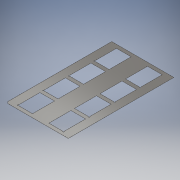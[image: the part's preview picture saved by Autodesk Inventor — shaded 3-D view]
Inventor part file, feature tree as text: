
AUTODESK INVENTOR PART (.ipt)
format: ipt  version: 2019.4 (Build 234330000, 330)  size: 232,960 bytes
history: native  units: in
note: dims shown in document units (in); Inventor stores cm internally (conversion verified against a paired STEP export)
features: extrude x2, sketch x2, chamfer x1
ambient origin geometry x8: Origin, YZ Plane, XZ Plane, XY Plane, X Axis, Y Axis, Z Axis, Center Point
bodies: Solid1 (feature_tree)
feature tree (5):
  extrude  "Extrusion1"  Depth=5.0in
  extrude  "Extrusion2"  Depth=1.1811in
  chamfer  "Chamfer1"  Distance=1.7717in
  sketch  "Sketch1"  dims[d0=8.5in d1=5.0in]
  sketch  "Sketch2"  dims[d2=0.0039in d3=0.0in d4=1.1811in d5=1.7717in d6=0.2835in d7=0.659in d8=0.0787in d9=0.0079in d18=0.0in d19=0.0in d20=0.0079in d21=1.5748in d23=2.0551in d24=0.7874in d26=2.5in d29=1.5748in d31=2.0551in d32=0.7874in d34=3.681in d37=0.6599in d38=0.125in d39=0.125in d40=45.0deg]
